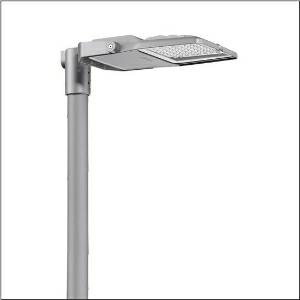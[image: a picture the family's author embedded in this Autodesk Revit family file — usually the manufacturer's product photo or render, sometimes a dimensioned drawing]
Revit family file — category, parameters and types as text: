
# Revit family: floodlight_fl_21_mini___pl52_5xa7775d2d3a_ca02
name_source: partatom
category: Lighting Fixtures
units: mm (PartAtom-declared; Revit-internal decimal feet)

## family parameters
Cut with Voids When Loaded = No
Host = Face
Light Source = No
Part Type = Normal
Room Calculation Point = No
Round Connector Dimension = Use Diameter
Shared = No

## types (1)
- --- (1 x LED, 17840 lm, 142.9 W, 3000K)
    Apparent Load = 143 VA
    CIE Flux Codes = 26 60 98 100 100
    Color Rendering = 70
    Color Temperature = 3000K
    Default Elevation = 1800 mm
    Description = Floodlight FL 21 mini, floodlight, primary light control with lens, of PMMA, primary optical cover: protective disc, of toughened safety glass, transparent, light distribution: PL52, light emission: direct distribution, installation type: surface-mounted, LED, High Power LED, rated luminous flux: 17.840lm, luminous efficacy: 125lm/W, light colour: 730, colour temperature: 3000K, control gear: Smart Interface (Zhaga), control: flexible luminous flux parameterisation, time-dependent luminous flux control, constant luminous flux control, overheat protection, pre-setting: logarithmic dimming characteristic, with terminal, 6-pole, mains connection: 220..240V, AC, 50/60Hz, start of lifetime: 143W, end of service life: 151W, reduction: 63W, luminaire housing, of diecast aluminium, powder-coated, Siteco® metallic grey (DB 702S), corrosivity category C5 mid according to DIN EN ISO 12944, suitable for swimming pools, chlorine-resistant, sealing non-destructively replaceable, please order mast flange separately, mast bracket, of steel, galvanised, powder-coated, Siteco® metallic grey (DB 702S), Smart Interface above, protection rating (complete): IP66, insulation class (complete): insulation class II (safety insulation), certification: CE, ENEC, VDE, protection symbol: D, impact resistance: IK08, permissible operating ambient temperature: -40..+40°C, permissible operating ambient temperature for outdoor applications: -40..+50°C, standard: DIN EN 12944, LABS conformity tested according to VDMA 24364:2018-05, packaging unit: 1 piece

Light Distribution: PL52
    Height = 70 mm
    Lamp = 1 x LED
    Lamp Light Flux = 17840 lm
    Lamp Power = 142.9 W
    Lamp count = 1
    Length = 485 mm
    Luminous efficacy = 125 lm/W
    Manufacturer = Siteco
    ModVariant = No
    Model = 5XA7775D2D3A
    Number of Poles = 1
    OnlyDefault = Yes
    Power Factor = 1
    Product Name = Floodlight FL 21 mini | PL52
    Product group = floodlight | pylon annexe
    ProductGroupID = 6200
    Protection Class = Protection class II
    Protection Degree = IP 66
    RLX_Detail_Level = 1
    RLX_Emergency_Light_Flux = 0 lm
    RLX_Emergency_Type = 0
    RLX_Emergency_Type_DB = No
    RlxData = <blob elided: 101581 chars, md5=4d90c762>
    Socket = socket
    Standby Power = 0 W
    System Light Flux = 17840 lm
    System Power = 143 W
    Type Comments = factory setting: luminous flux: 100 % | dim-lin: 254 | 730 mA
    Type Image = l_1007125.jpg
    URL = http://relux.com
    VarID = @adj_163186
    Voltage = 0 V
    Weight = 0.00 kg
    Width = 337 mm

## geometry (parser evidence)
native form markers: Blend x4, Sweep x12
no freeform markers — native parametric forms only
